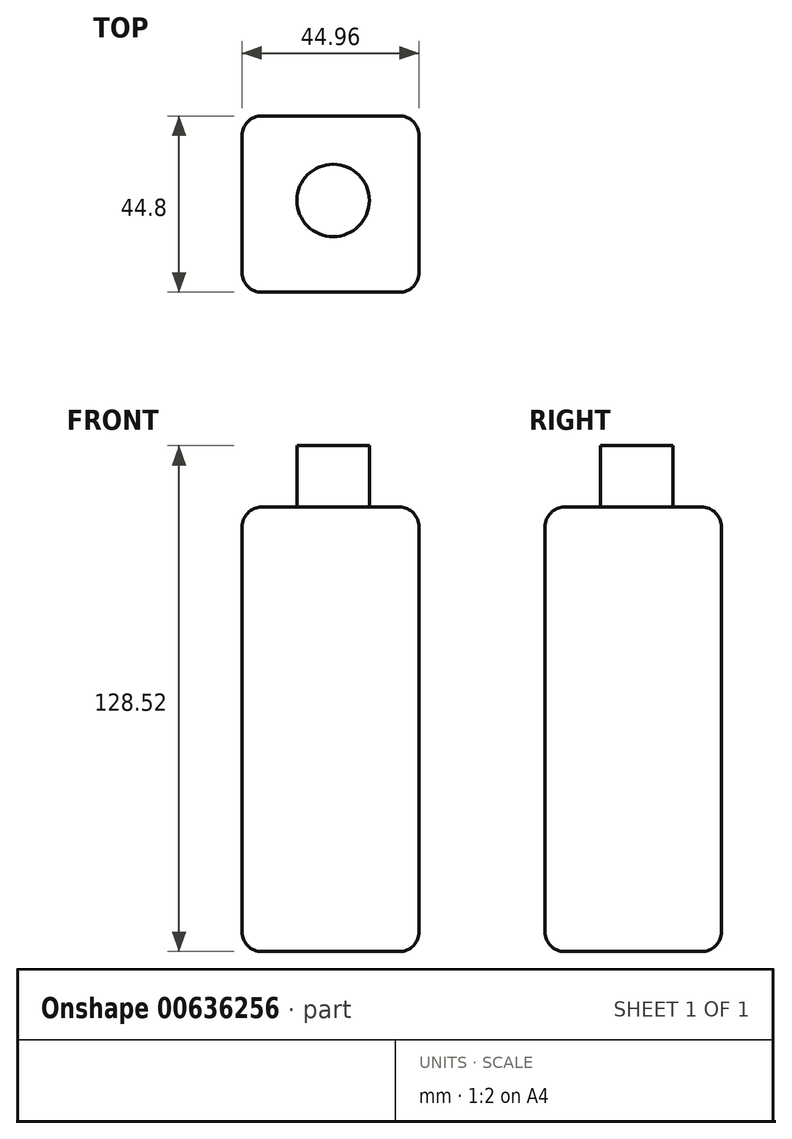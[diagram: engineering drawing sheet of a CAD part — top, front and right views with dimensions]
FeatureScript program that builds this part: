
annotation { "Feature Type Name" : "Feature", "Feature Type Description" : "" }
export const myFeature = defineFeature(function(context is Context, id is Id, definition is map)
    precondition{}
    {
        {
            var Q0;
            Q0=qCreatedBy(makeId("Front.planeOp"),FACE);
            var sketch = newSketch(context, id + "F0", { "sketchPlane" : qUnion([Q0])});
            skLineSegment(sketch, "E0.bottom", {"start": v(-22, 56.26) * mm, "end": v(22.95, 56.26) * mm});
            skLineSegment(sketch, "E0.top", {"start": v(-22, -56.66) * mm, "end": v(22.95, -56.66) * mm});
            skLineSegment(sketch, "E0.left", {"start": v(-22, 56.26) * mm, "end": v(-22, -56.66) * mm});
            skLineSegment(sketch, "E0.right", {"start": v(22.95, 56.26) * mm, "end": v(22.95, -56.66) * mm});
            skSolve(sketch);
        }
        {
            var Q0;
            Q0=makeQuery(id+"F0.imprint","IMPRINT",FACE,{"disambiguationData":[TD([[makeQuery(id+"F0.imprint","IMPRINT",EDGE,{"derivedFrom":sQuery(id+"F0.wireOp",EDGE,"E0.bottom")}),-1.0]])]});
            extrude(context, id + "F1", {"entities" : qUnion([Q0]), "depth" : 44.8 * mm, "offsetDistance" : 25 * mm});
        }
        {
            var Q0;
            Q0=makeQuery(id+"F1.opExtrude","SWEPT_EDGE",EDGE,{"disambiguationData":[OSD([sQuery(id+"F0.wireOp",EDGE,"E0.bottom"),sQuery(id+"F0.wireOp",EDGE,"E0.right")])]});
            var Q1;
            Q1=makeQuery(id+"F1.opExtrude","CAP_EDGE",EDGE,{"disambiguationData":[OSD([sQuery(id+"F0.wireOp",EDGE,"E0.bottom")])],"isStart":true});
            var Q2;
            Q2=makeQuery(id+"F1.opExtrude","SWEPT_EDGE",EDGE,{"disambiguationData":[OSD([sQuery(id+"F0.wireOp",EDGE,"E0.bottom"),sQuery(id+"F0.wireOp",EDGE,"E0.left")])]});
            var Q3;
            Q3=makeQuery(id+"F1.opExtrude","CAP_EDGE",EDGE,{"disambiguationData":[OSD([sQuery(id+"F0.wireOp",EDGE,"E0.bottom")])],"isStart":false});
            var Q4;
            Q4=makeQuery(id+"F1.opExtrude","SWEPT_EDGE",EDGE,{"disambiguationData":[OSD([sQuery(id+"F0.wireOp",EDGE,"E0.top"),sQuery(id+"F0.wireOp",EDGE,"E0.right")])]});
            var Q5;
            Q5=makeQuery(id+"F1.opExtrude","CAP_EDGE",EDGE,{"disambiguationData":[OSD([sQuery(id+"F0.wireOp",EDGE,"E0.right")])],"isStart":false});
            var Q6;
            Q6=makeQuery(id+"F1.opExtrude","CAP_EDGE",EDGE,{"disambiguationData":[OSD([sQuery(id+"F0.wireOp",EDGE,"E0.right")])],"isStart":true});
            var Q7;
            Q7=makeQuery(id+"F1.opExtrude","CAP_FACE",FACE,{"disambiguationData":[OSD([sQuery(id+"F0.wireOp",EDGE,"E0.bottom"),sQuery(id+"F0.wireOp",EDGE,"E0.top"),sQuery(id+"F0.wireOp",EDGE,"E0.left"),sQuery(id+"F0.wireOp",EDGE,"E0.right")])],"isStart":true});
            var Q8;
            Q8=makeQuery(id+"F1.opExtrude","CAP_EDGE",EDGE,{"disambiguationData":[OSD([sQuery(id+"F0.wireOp",EDGE,"E0.left")])],"isStart":false});
            var Q9;
            Q9=makeQuery(id+"F1.opExtrude","SWEPT_EDGE",EDGE,{"disambiguationData":[OSD([sQuery(id+"F0.wireOp",EDGE,"E0.top"),sQuery(id+"F0.wireOp",EDGE,"E0.left")])]});
            var Q10;
            Q10=makeQuery(id+"F1.opExtrude","CAP_EDGE",EDGE,{"disambiguationData":[OSD([sQuery(id+"F0.wireOp",EDGE,"E0.top")])],"isStart":false});
            fillet(context, id + "F2", {"entities" : qUnion([Q0, Q1, Q2, Q3, Q4, Q5, Q6, Q7, Q8, Q9, Q10]), "radius" : 5 * mm, "tangentPropagation" : true, "allowEdgeOverflow" : false});
        }
        {
            var Q0;
            Q0=makeQuery(id+"F1.opExtrude","SWEPT_FACE",FACE,{"disambiguationData":[OSD([sQuery(id+"F0.wireOp",EDGE,"E0.bottom")])]});
            var sketch = newSketch(context, id + "F3", { "sketchPlane" : qUnion([Q0])});
            skCircle(sketch, "E1", {"center": v(1.11, -21.47) * mm, "radius": 9.2 * mm});
            skSolve(sketch);
        }
        {
            var Q0;
            Q0=makeQuery(id+"F3.imprint","IMPRINT",FACE,{"disambiguationData":[TD([[makeQuery(id+"F3.imprint","IMPRINT",EDGE,{"derivedFrom":sQuery(id+"F3.wireOp",EDGE,"E1")}),1.0]])]});
            extrude(context, id + "F4", {"entities" : qUnion([Q0]), "operationType" : NewBodyOperationType.ADD, "depth" : 15.6 * mm, "offsetDistance" : 25 * mm});
        }
    });
